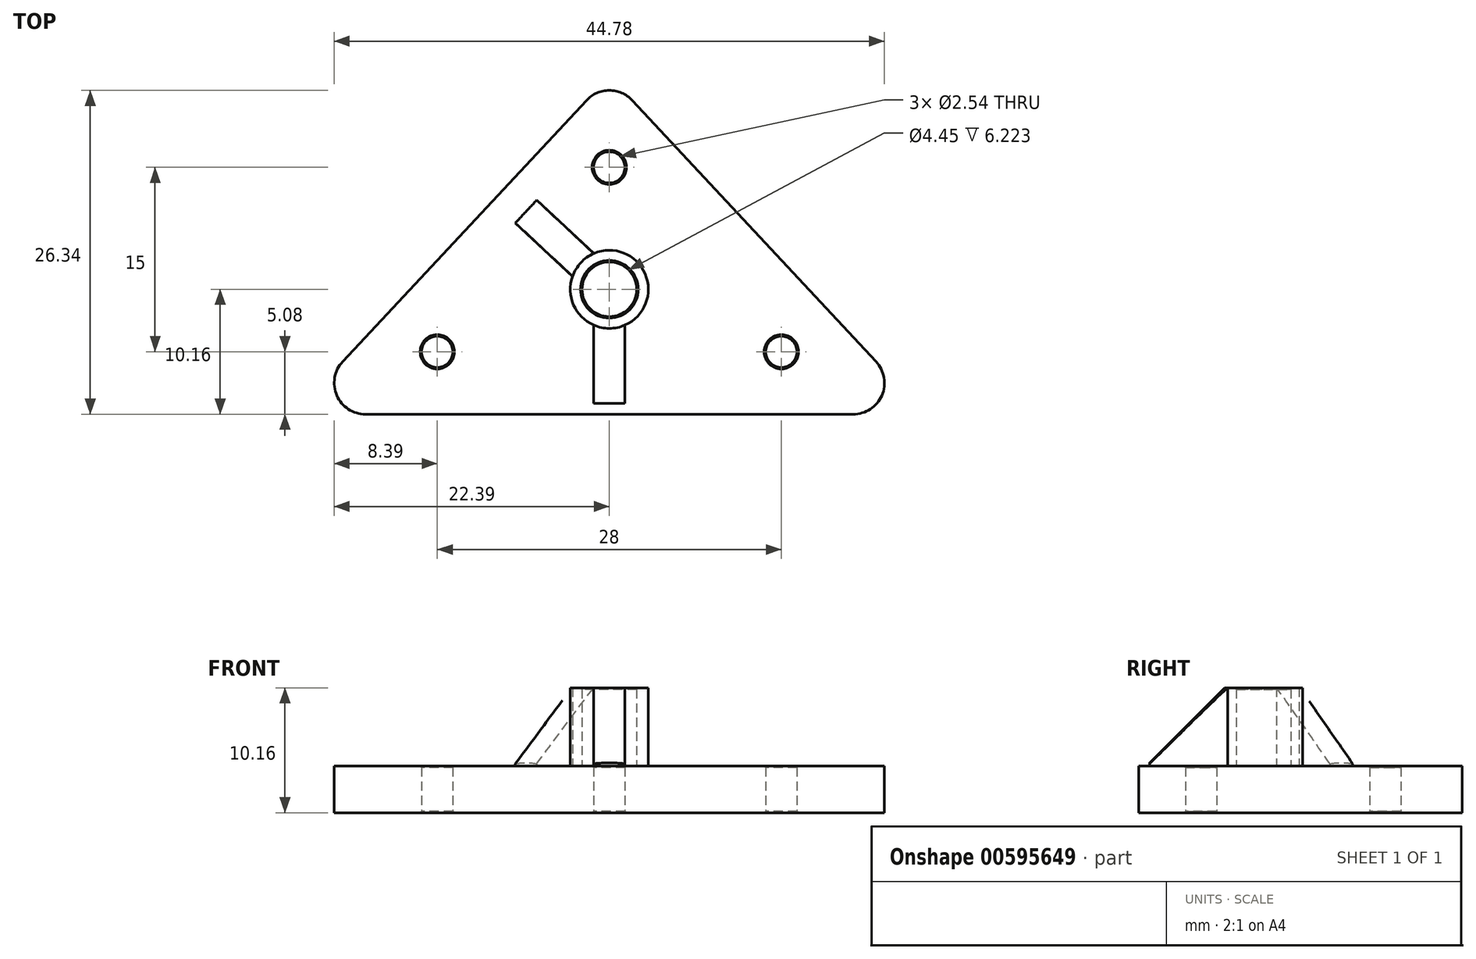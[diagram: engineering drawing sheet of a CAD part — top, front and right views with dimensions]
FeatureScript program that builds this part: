
annotation { "Feature Type Name" : "Feature", "Feature Type Description" : "" }
export const myFeature = defineFeature(function(context is Context, id is Id, definition is map)
    precondition{}
    {
        {
            var Q0;
            Q0=qCreatedBy(makeId("Top.planeOp"),FACE);
            var sketch = newSketch(context, id + "F0", { "sketchPlane" : qUnion([Q0])});
            skLineSegment(sketch, "E0", {"start": v(0, 0) * mm, "end": v(-14, -15) * mm});
            skLineSegment(sketch, "E1", {"start": v(-14, -15) * mm, "end": v(14, -15) * mm});
            skLineSegment(sketch, "E2", {"start": v(14, -15) * mm, "end": v(0, 0) * mm});
            skLineSegment(sketch, "E3.0", {"start": v(0, 7.45) * mm, "end": v(-25.7, -20.08) * mm});
            skLineSegment(sketch, "E3.1", {"start": v(25.7, -20.08) * mm, "end": v(0, 7.45) * mm});
            skLineSegment(sketch, "E3.2", {"start": v(-25.7, -20.08) * mm, "end": v(25.7, -20.08) * mm});
            skCircle(sketch, "E4", {"center": v(-14, -15) * mm, "radius": 1.27 * mm});
            skCircle(sketch, "E5", {"center": v(14, -15) * mm, "radius": 1.27 * mm});
            skCircle(sketch, "E6", {"center": v(0, 0) * mm, "radius": 1.27 * mm});
            skSolve(sketch);
        }
        {
            var Q0;
            {var subQ1=sQuery(id+"F0.wireOp",EDGE,"E0");var subQ5=sQuery(id+"F0.wireOp",EDGE,"E6");var subQ6=makeQuery(id+"F0.imprint","INTERSECT",VERTEX,{"derivedFrom":[subQ1,subQ5]});Q0=makeQuery(id+"F0.imprint","IMPRINT",FACE,{"disambiguationData":[TD([[makeQuery(id+"F0.imprint","IMPRINT",EDGE,{"disambiguationData":[TD([[subQ6,-1.0]])],"derivedFrom":subQ1}),1.0]])]});}
            var Q1;
            Q1=makeQuery(id+"F0.imprint","IMPRINT",FACE,{"disambiguationData":[TD([[makeQuery(id+"F0.imprint","IMPRINT",EDGE,{"derivedFrom":sQuery(id+"F0.wireOp",EDGE,"E3.0")}),1.0]])]});
            extrude(context, id + "F1", {"entities" : qUnion([Q0, Q1]), "depth" : 3.8 * mm, "offsetDistance" : 25.4 * mm});
        }
        {
            var Q0;
            Q0=makeQuery(id+"F1.opExtrude","SWEPT_EDGE",EDGE,{"disambiguationData":[OSD([sQuery(id+"F0.wireOp",EDGE,"E3.0"),sQuery(id+"F0.wireOp",EDGE,"E3.2")])]});
            var Q1;
            Q1=makeQuery(id+"F1.opExtrude","SWEPT_EDGE",EDGE,{"disambiguationData":[OSD([sQuery(id+"F0.wireOp",EDGE,"E3.1"),sQuery(id+"F0.wireOp",EDGE,"E3.2")])]});
            var Q2;
            Q2=makeQuery(id+"F1.opExtrude","SWEPT_EDGE",EDGE,{"disambiguationData":[OSD([sQuery(id+"F0.wireOp",EDGE,"E3.0"),sQuery(id+"F0.wireOp",EDGE,"E3.1")])]});
            fillet(context, id + "F2", {"entities" : qUnion([Q0, Q1, Q2]), "radius" : 2.54 * mm, "tangentPropagation" : true, "allowEdgeOverflow" : false});
        }
        {
            var Q0;
            Q0=makeQuery(id+"F1.opExtrude","SWEPT_FACE",FACE,{"disambiguationData":[OSD([sQuery(id+"F0.wireOp",EDGE,"E4")])]});
            var Q1;
            Q1=makeQuery(id+"F1.opExtrude","SWEPT_FACE",FACE,{"disambiguationData":[OSD([sQuery(id+"F0.wireOp",EDGE,"E5")])]});
            var Q2;
            Q2=makeQuery(id+"F1.opExtrude","SWEPT_FACE",FACE,{"disambiguationData":[OSD([sQuery(id+"F0.wireOp",EDGE,"E6")])]});
            chamfer(context, id + "F3", {"entities" : qUnion([Q0, Q1, Q2]), "width" : 0.13 * mm, "tangentPropagation" : true});
        }
        {
            var Q0;
            Q0=makeQuery(id+"F1.opExtrude","CAP_FACE",FACE,{"disambiguationData":[OSD([sQuery(id+"F0.wireOp",EDGE,"E3.0"),sQuery(id+"F0.wireOp",EDGE,"E3.1"),sQuery(id+"F0.wireOp",EDGE,"E3.2"),sQuery(id+"F0.wireOp",EDGE,"E4"),sQuery(id+"F0.wireOp",EDGE,"E5"),sQuery(id+"F0.wireOp",EDGE,"E6")])],"isStart":false});
            var sketch = newSketch(context, id + "F4", { "sketchPlane" : qUnion([Q0])});
            skCircle(sketch, "E7", {"center": v(0, -9.92) * mm, "radius": 3.18 * mm});
            skLineSegment(sketch, "E8", {"start": v(-7.64, -4.52) * mm, "end": v(-3, -8.86) * mm});
            skLineSegment(sketch, "E9", {"start": v(-7.64, -4.52) * mm, "end": v(-5.91, -2.67) * mm});
            skLineSegment(sketch, "E10", {"start": v(-5.91, -2.67) * mm, "end": v(-1.26, -7) * mm});
            skLineSegment(sketch, "E11", {"start": v(0, -9.92) * mm, "end": v(-6.78, -3.6) * mm, "construction": true});
            skCircle(sketch, "E12", {"center": v(0, -9.92) * mm, "radius": 2.22 * mm});
            skLineSegment(sketch, "E13", {"start": v(-1.27, -12.83) * mm, "end": v(-1.27, -19.2) * mm});
            skLineSegment(sketch, "E14", {"start": v(-1.27, -19.2) * mm, "end": v(1.27, -19.2) * mm});
            skLineSegment(sketch, "E15", {"start": v(1.27, -19.2) * mm, "end": v(1.27, -12.83) * mm});
            skLineSegment(sketch, "E16", {"start": v(0, -9.92) * mm, "end": v(0, -19.2) * mm, "construction": true});
            skSolve(sketch);
        }
        {
            var Q0;
            Q0=makeQuery(id+"F4.imprint","IMPRINT",FACE,{"disambiguationData":[TD([[makeQuery(id+"F4.imprint","IMPRINT",EDGE,{"derivedFrom":sQuery(id+"F4.wireOp",EDGE,"E12")}),-1.0]])]});
            var Q1;
            {var subQ0=sQuery(id+"F4.wireOp",EDGE,"E8");Q1=makeQuery(id+"F4.imprint","IMPRINT",FACE,{"disambiguationData":[TD([[makeQuery(id+"F4.imprint","IMPRINT",EDGE,{"derivedFrom":subQ0}),1.0]])]});}
            var Q2;
            {var subQ0=sQuery(id+"F4.wireOp",EDGE,"E13");Q2=makeQuery(id+"F4.imprint","IMPRINT",FACE,{"disambiguationData":[TD([[makeQuery(id+"F4.imprint","IMPRINT",EDGE,{"derivedFrom":subQ0}),1.0]])]});}
            extrude(context, id + "F5", {"entities" : qUnion([Q0, Q1, Q2]), "operationType" : NewBodyOperationType.ADD, "depth" : 6.35 * mm, "offsetDistance" : 25.4 * mm});
        }
        {
            var Q0;
            {var subQ0=sQuery(id+"F4.wireOp",EDGE,"E15");var subQ1=sQuery(id+"F4.wireOp",EDGE,"E14");var subQ2=sQuery(id+"F4.wireOp",EDGE,"E13");var subQ3=sQuery(id+"F4.wireOp",EDGE,"E12");var subQ4=sQuery(id+"F4.wireOp",EDGE,"E10");var subQ5=sQuery(id+"F4.wireOp",EDGE,"E9");var subQ6=sQuery(id+"F4.wireOp",EDGE,"E8");var subQ7=sQuery(id+"F4.wireOp",EDGE,"E7");Q0=makeQuery(id+"FYvwpGSAQ1wOhRa_1.1.F5.boolean.opBoolean","MERGE",FACE,{"derivedFrom":[makeQuery(id+"F5.opExtrude","CAP_FACE",FACE,{"disambiguationData":[OSD([subQ7,subQ6,subQ5,subQ4,subQ3,subQ2,subQ1,subQ0])],"isStart":false}),makeQuery(id+"FYvwpGSAQ1wOhRa_1.1.F5.opExtrude","CAP_FACE",FACE,{"disambiguationData":[OSD([subQ7,subQ6,subQ5,subQ4,subQ3,subQ2,subQ1,subQ0])],"isStart":false})]});}
            var sketch = newSketch(context, id + "F6", { "sketchPlane" : qUnion([Q0])});
            skPoint(sketch, "E17", {"position": v(0, -9.92) * mm});
            skSolve(sketch);
        }
        {
            var Q0;
            Q0=qCreatedBy(makeId("Right.planeOp"),FACE);
            var sketch = newSketch(context, id + "F7", { "sketchPlane" : qUnion([Q0])});
            skPoint(sketch, "E18.0", {"position": v(-9.92, 10.16) * mm});
            skLineSegment(sketch, "E19.bottom", {"start": v(-9.92, 10.16) * mm, "end": v(-6.74, 10.16) * mm, "construction": true});
            skLineSegment(sketch, "E19.left", {"start": v(-9.92, 10.16) * mm, "end": v(-9.92, 14.55) * mm, "construction": true});
            skPoint(sketch, "E20.0", {"position": v(-6.74, 10.16) * mm});
            skLineSegment(sketch, "E21.0", {"start": v(5.46, 3.81) * mm, "end": v(-0.9, 3.81) * mm});
            skLineSegment(sketch, "E22", {"start": v(-0.9, 3.81) * mm, "end": v(-6.75, 3.81) * mm});
            skLineSegment(sketch, "E23", {"start": v(-6.74, 10.16) * mm, "end": v(-0.4, 3.8) * mm});
            skLineSegment(sketch, "E24.trimOffspring", {"start": v(-6.75, 3.81) * mm, "end": v(-15.8, 3.81) * mm});
            skLineSegment(sketch, "E25", {"start": v(2.63, 10.16) * mm, "end": v(-6.74, 10.16) * mm});
            skLineSegment(sketch, "E26", {"start": v(-0.4, 3.81) * mm, "end": v(2.63, 3.81) * mm});
            skLineSegment(sketch, "E27", {"start": v(2.63, 3.81) * mm, "end": v(2.63, 10.16) * mm});
            skSolve(sketch);
        }
        {
            var Q0;
            Q0 = qSketchRegion(id + "F7", true);
            var Q1;
            Q1=sQuery(id+"F7.wireOp",EDGE,"E19.left");
            revolve(context, id + "F8", {"operationType" : NewBodyOperationType.REMOVE, "surfaceOperationType" : NewSurfaceOperationType.NEW, "entities" : qUnion([Q0]), "axis" : qUnion([Q1]), "revolveType" : RevolveType.FULL, "oppositeDirection" : true});
        }
        {
            var Q0;
            Q0=makeQuery(id+"F5.opExtrude","CAP_EDGE",EDGE,{"disambiguationData":[OSD([sQuery(id+"F4.wireOp",EDGE,"E12")])],"isStart":false});
            chamfer(context, id + "F9", {"entities" : qUnion([Q0]), "width" : 0.13 * mm, "tangentPropagation" : true});
        }
    });
